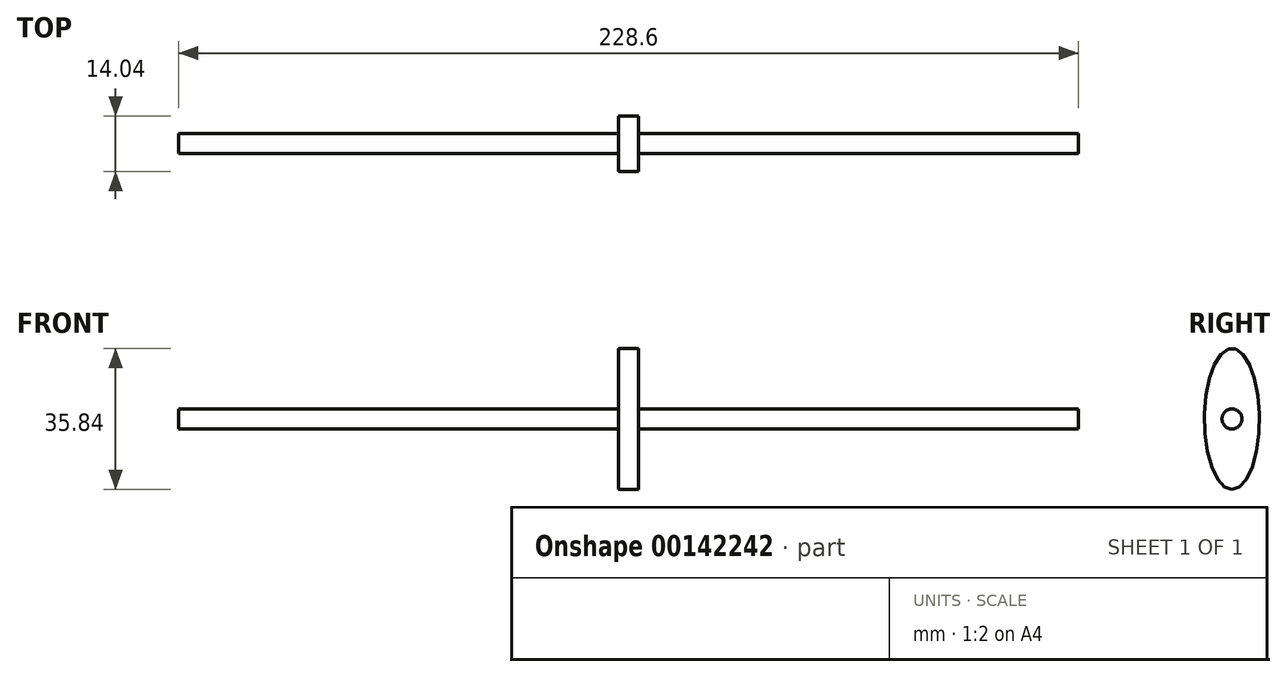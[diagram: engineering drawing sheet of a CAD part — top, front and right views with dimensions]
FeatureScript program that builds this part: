
annotation { "Feature Type Name" : "Feature", "Feature Type Description" : "" }
export const myFeature = defineFeature(function(context is Context, id is Id, definition is map)
    precondition{}
    {
        {
            var Q0;
            Q0=qCreatedBy(makeId("Right.planeOp"),FACE);
            var sketch = newSketch(context, id + "F0", { "sketchPlane" : qUnion([Q0])});
            skCircle(sketch, "E0", {"center": v(0, 0) * mm, "radius": 2.54 * mm});
            skSolve(sketch);
        }
        {
            var Q0;
            Q0 = qSketchRegion(id + "F0", true);
            extrude(context, id + "F1", {"entities" : qUnion([Q0]), "endBound" : BoundingType.SYMMETRIC, "depth" : 228.6 * mm});
        }
        {
            var Q0;
            Q0=qCreatedBy(makeId("Right.planeOp"),FACE);
            var sketch = newSketch(context, id + "F2", { "sketchPlane" : qUnion([Q0])});
            skEllipse(sketch, "E1", {"center": v(0, 0) * mm, "majorRadius": 17.92 * mm, "minorRadius": 7.02 * mm, "majorAxis": v(0, -1)});
            skSolve(sketch);
        }
        {
            var Q0;
            Q0 = qSketchRegion(id + "F2", true);
            extrude(context, id + "F3", {"entities" : qUnion([Q0]), "operationType" : NewBodyOperationType.ADD, "endBound" : BoundingType.SYMMETRIC, "depth" : 5.08 * mm});
        }
    });
